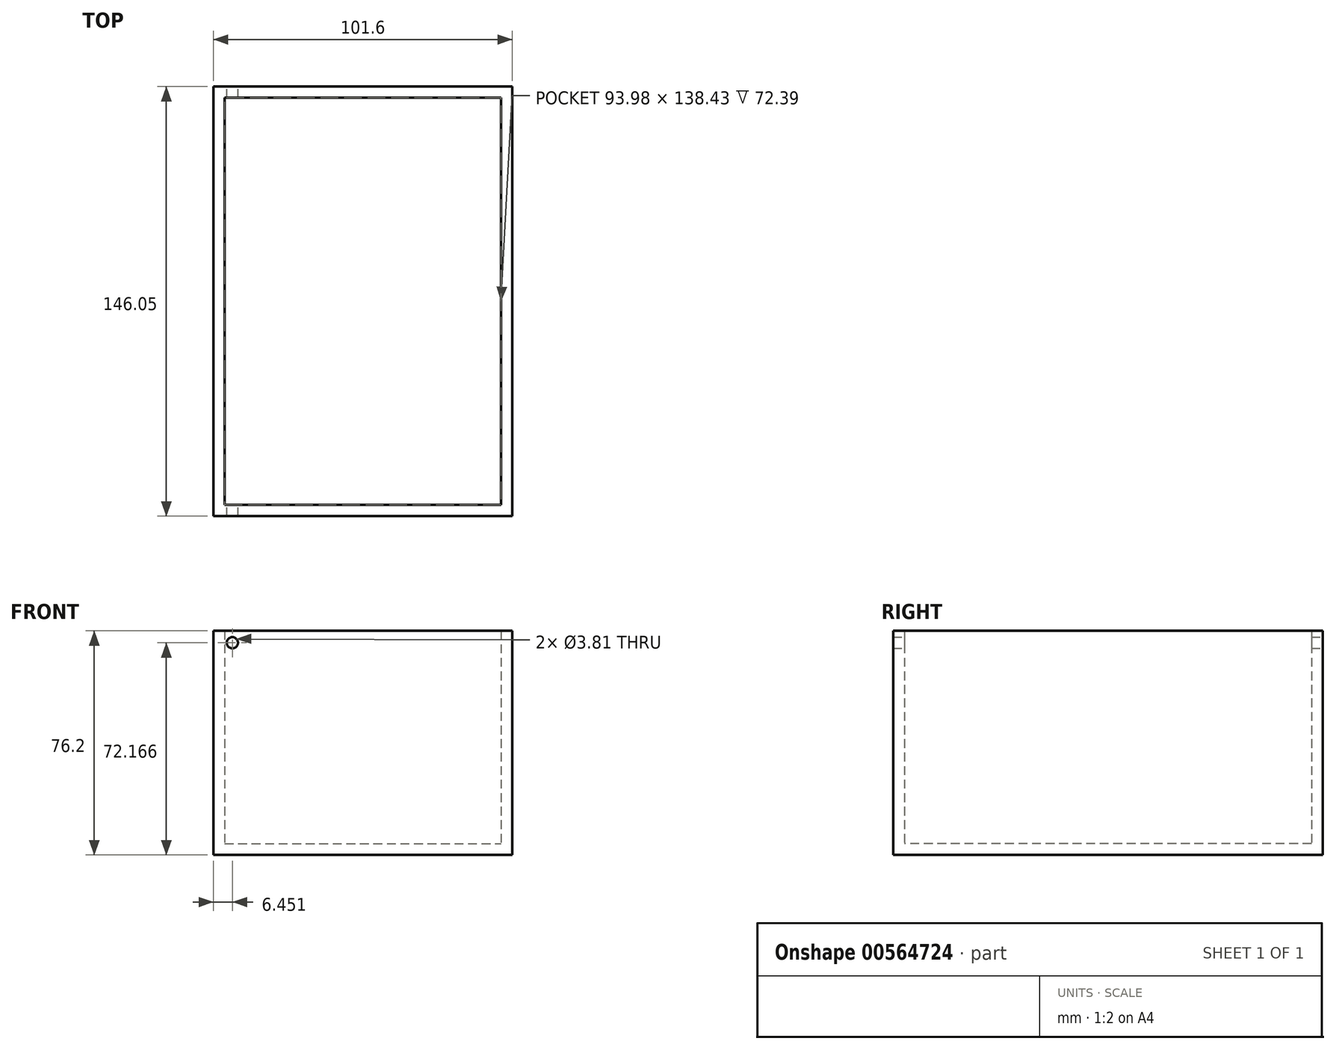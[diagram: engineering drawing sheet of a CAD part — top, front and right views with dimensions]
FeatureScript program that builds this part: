
annotation { "Feature Type Name" : "Feature", "Feature Type Description" : "" }
export const myFeature = defineFeature(function(context is Context, id is Id, definition is map)
    precondition{}
    {
        {
            var Q0;
            Q0=qCreatedBy(makeId("Top.planeOp"),FACE);
            var sketch = newSketch(context, id + "F0", { "sketchPlane" : qUnion([Q0])});
            skLineSegment(sketch, "E0.bottom", {"start": v(-66, 71.12) * mm, "end": v(35.6, 71.12) * mm});
            skLineSegment(sketch, "E0.top", {"start": v(-66, -74.93) * mm, "end": v(35.6, -74.93) * mm});
            skLineSegment(sketch, "E0.left", {"start": v(-66, 71.12) * mm, "end": v(-66, -74.93) * mm});
            skLineSegment(sketch, "E0.right", {"start": v(35.6, 71.12) * mm, "end": v(35.6, -74.93) * mm});
            skSolve(sketch);
        }
        {
            var Q0;
            Q0=makeQuery(id+"F0.imprint","IMPRINT",FACE,{"disambiguationData":[TD([[makeQuery(id+"F0.imprint","IMPRINT",EDGE,{"derivedFrom":sQuery(id+"F0.wireOp",EDGE,"E0.bottom")}),-1.0]])]});
            extrude(context, id + "F1", {"entities" : qUnion([Q0]), "depth" : 76.2 * mm, "offsetDistance" : 25.4 * mm});
        }
        {
            var Q0;
            Q0=makeQuery(id+"F1.opExtrude","CAP_FACE",FACE,{"disambiguationData":[OSD([sQuery(id+"F0.wireOp",EDGE,"E0.bottom"),sQuery(id+"F0.wireOp",EDGE,"E0.top"),sQuery(id+"F0.wireOp",EDGE,"E0.left"),sQuery(id+"F0.wireOp",EDGE,"E0.right")])],"isStart":false});
            shell(context, id + "F2", {"entities" : qUnion([Q0]), "thickness" : 3.8 * mm});
        }
        {
            var Q0;
            Q0=makeQuery(id+"F1.opExtrude","SWEPT_FACE",FACE,{"disambiguationData":[OSD([sQuery(id+"F0.wireOp",EDGE,"E0.bottom")])]});
            var sketch = newSketch(context, id + "F3", { "sketchPlane" : qUnion([Q0])});
            skPoint(sketch, "E1", {"position": v(59.55, 72.17) * mm});
            skSolve(sketch);
        }
        {
            var Q0;
            Q0=sQuery(id+"F3.wireOp",VERTEX,"E1");
            var Q1;
            Q1=makeQuery(id+"F1.opExtrude","SWEPT_BODY",BODY,{"disambiguationData":[OSD([sQuery(id+"F0.wireOp",EDGE,"E0.bottom"),sQuery(id+"F0.wireOp",EDGE,"E0.top"),sQuery(id+"F0.wireOp",EDGE,"E0.left"),sQuery(id+"F0.wireOp",EDGE,"E0.right")])]});
            hole(context, id + "F4", {"style" : HoleStyle.SIMPLE, "endStyle" : HoleEndStyle.THROUGH, "holeDiameter" : 3.8 * mm, "isTappedThrough" : true, "tappedDepth" : 12.7 * mm, "tapClearance" : 3, "locations" : qUnion([Q0]), "scope" : qUnion([Q1])});
        }
    });
